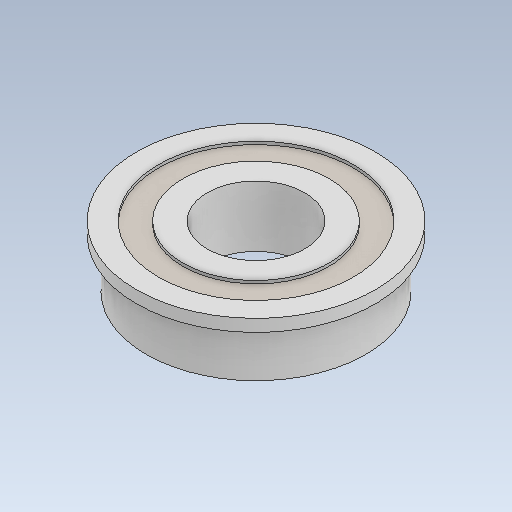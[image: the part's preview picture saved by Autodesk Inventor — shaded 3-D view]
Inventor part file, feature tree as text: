
AUTODESK INVENTOR PART (.ipt)
format: ipt  version: 2020 (Build 240168000, 168)  size: 143,360 bytes
history: native  units: in
note: dims shown in document units (in); Inventor stores cm internally (conversion verified against a paired STEP export)
features: revolve x1
ambient origin geometry x8: Origin, YZ Plane, XZ Plane, XY Plane, X Axis, Y Axis, Z Axis, Center Point
bodies: Solid1 (feature_tree)
feature tree (1):
  revolve  "Revolve1"  [1 undecoded]
note: 1 required parameter value undecoded (feature->parameter linkage not recoverable at this tier; creation-order binding heuristic only, values carry confidence <= 0.55)
